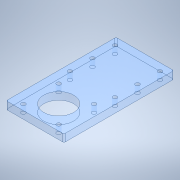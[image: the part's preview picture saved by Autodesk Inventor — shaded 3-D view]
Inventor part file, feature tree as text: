
AUTODESK INVENTOR PART (.ipt)
format: ipt  version: 2022 (Build 260153000, 153)  size: 243,200 bytes
history: native  units: mm
features: extrude x6, sketch x6, fillet x1
ambient origin geometry x8: Origin, YZ Plane, XZ Plane, XY Plane, X Axis, Y Axis, Z Axis, Center Point
bodies: Solid1 (feature_tree)
feature tree (13):
  extrude  "Extrusion1"  Depth=40.0mm
  extrude  "Extrusion2"  Depth=10.0mm TaperAngle=0.0deg
  sketch  "Sketch5"  dims[d5=145.0mm d6=0.0mm]
  extrude  "Extrusion3"  TaperAngle=0.0deg  [1 undecoded]
  extrude  "Extrusion4"  Depth=2.0mm
  extrude  "Extrusion5"  Depth=5.5mm
  extrude  "Extrusion6"  Depth=2.0mm
  fillet  "Fillet1"  Radius=5.5mm
  sketch  "Sketch1"  dims[d0=40.0mm d1=40.0mm]
  sketch  "Sketch3"  dims[d2=2.0mm d3=10.0mm d4=0.0mm]
  sketch  "Sketch6"  dims[d7=2.0mm d13=5.5mm]
  sketch  "Sketch7"  dims[d14=5.5mm d15=5.5mm]
  sketch  "Sketch8"  dims[d16=5.5mm d17=5.5mm d18=5.5mm d20=40.0mm d21=5.5mm d22=5.5mm d23=5.5mm d24=5.5mm d25=10.0mm d26=0.0mm d27=6.0mm d28=0.0mm d29=10.0mm d30=0.0mm d31=4.0mm d32=0.0mm d33=0.0mm d34=0.0mm d35=2.0mm]
note: 1 required parameter value undecoded (feature->parameter linkage not recoverable at this tier; creation-order binding heuristic only, values carry confidence <= 0.55)
